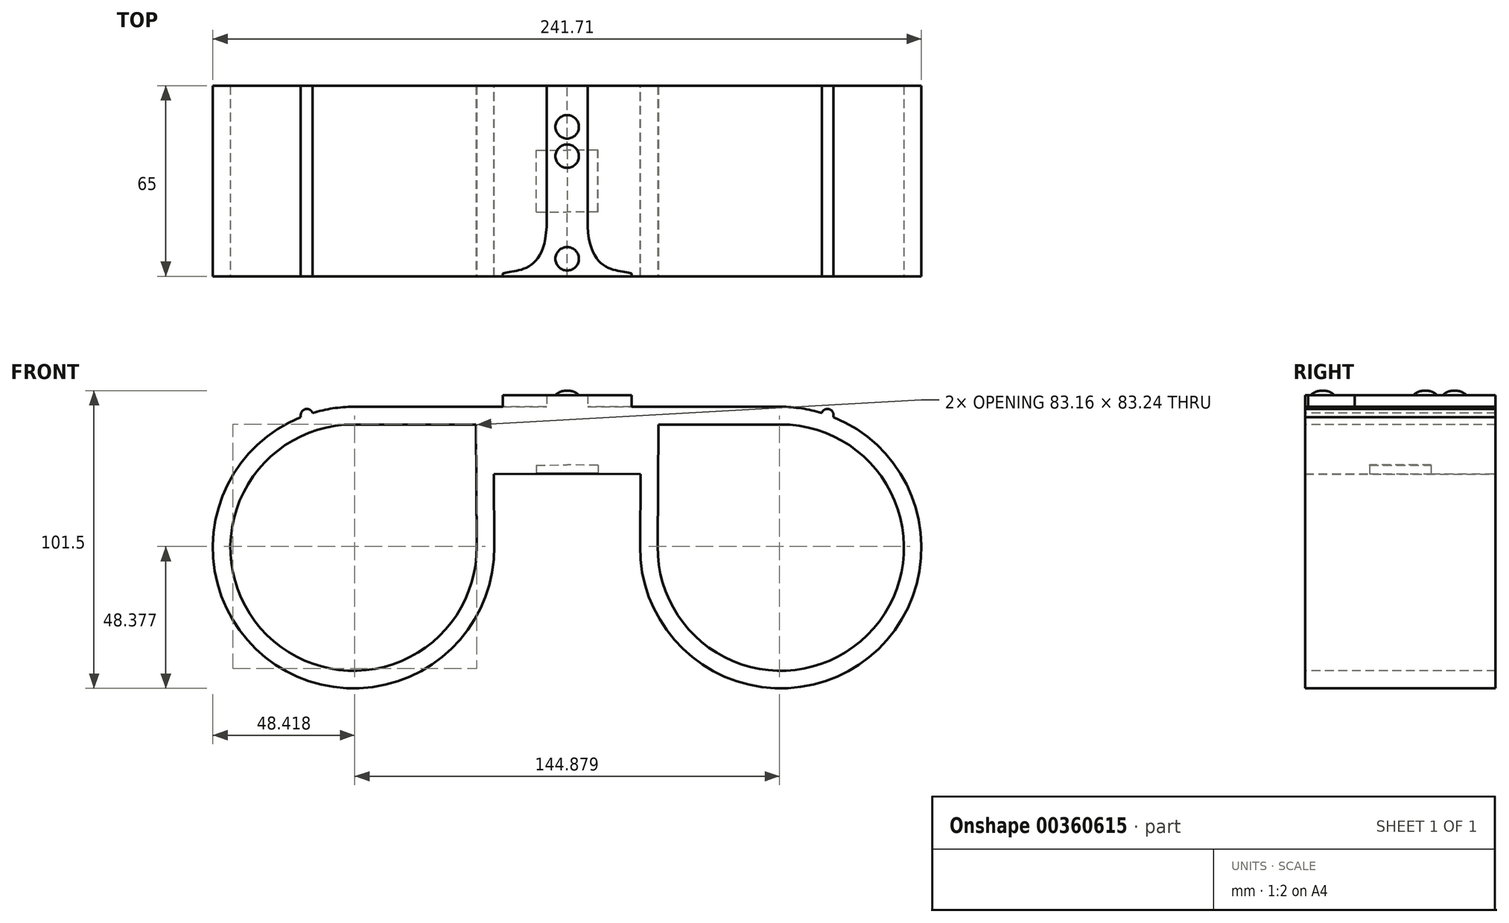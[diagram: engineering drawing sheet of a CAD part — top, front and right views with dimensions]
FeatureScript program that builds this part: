
annotation { "Feature Type Name" : "Feature", "Feature Type Description" : "" }
export const myFeature = defineFeature(function(context is Context, id is Id, definition is map)
    precondition{}
    {
        {
            var Q0;
            Q0=qCreatedBy(makeId("Front.planeOp"),FACE);
            var sketch = newSketch(context, id + "F0", { "sketchPlane" : qUnion([Q0])});
            skLineSegment(sketch, "E0", {"start": v(42.77, 0.25) * mm, "end": v(42.77, 23.06) * mm});
            skLineSegment(sketch, "E1", {"start": v(42.77, 23.06) * mm, "end": v(-30.09, 23.06) * mm});
            skLineSegment(sketch, "E2", {"start": v(-30.09, 23.06) * mm, "end": v(-30.09, -24.94) * mm});
            skLineSegment(sketch, "E3", {"start": v(0, 0) * mm, "end": v(17.77, 0.1) * mm});
            skCircle(sketch, "E4", {"center": v(-30.09, -24.94) * mm, "radius": 48 * mm});
            skLineSegment(sketch, "E5", {"start": v(17.91, -24.83) * mm, "end": v(17.77, 0.12) * mm});
            skPoint(sketch, "E5.endSnap0", {"position": v(21.38, 0.12) * mm});
            skLineSegment(sketch, "E6", {"start": v(17.77, 0.1) * mm, "end": v(42.77, 0.25) * mm});
            skSolve(sketch);
        }
        {
            var Q0;
            Q0 = qSketchRegion(id + "F0", true);
            extrude(context, id + "F1", {"entities" : qUnion([Q0]), "depth" : 65 * mm});
        }
        {
            var Q0;
            Q0=makeQuery(id+"F1.opExtrude","CAP_FACE",FACE,{"disambiguationData":[OSD([sQuery(id+"F0.wireOp",EDGE,"E0"),sQuery(id+"F0.wireOp",EDGE,"E1"),sQuery(id+"F0.wireOp",EDGE,"E4"),sQuery(id+"F0.wireOp",EDGE,"E5"),sQuery(id+"F0.wireOp",EDGE,"E6")])],"isStart":false});
            var sketch = newSketch(context, id + "F2", { "sketchPlane" : qUnion([Q0])});
            skCircle(sketch, "E7", {"center": v(-30.09, -24.94) * mm, "radius": 48 * mm});
            skPoint(sketch, "E7.first.point", {"position": v(-58.46, 13.77) * mm});
            skPoint(sketch, "E7.second.point", {"position": v(2.11, -60.54) * mm});
            skPoint(sketch, "E7.third.point", {"position": v(-63.88, -59.04) * mm});
            skLineSegment(sketch, "E8", {"start": v(-30.09, -24.94) * mm, "end": v(-30.09, 32.11) * mm, "construction": true});
            skLineSegment(sketch, "E9", {"start": v(-30.09, -24.94) * mm, "end": v(-44.09, -24.94) * mm});
            skLineSegment(sketch, "E10", {"start": v(-44.09, -24.94) * mm, "end": v(-44.09, 50.31) * mm});
            skLineSegment(sketch, "E11", {"start": v(-44.09, -24.94) * mm, "end": v(-48.09, -24.94) * mm});
            skLineSegment(sketch, "E12", {"start": v(-48.09, -24.94) * mm, "end": v(-48.09, 37.37) * mm});
            skCircle(sketch, "E13", {"center": v(-30.09, -24.94) * mm, "radius": 50 * mm});
            skSolve(sketch);
        }
        {
            var Q0;
            {var subQ0=sQuery(id+"F2.wireOp",EDGE,"E10");var subQ1=sQuery(id+"F2.wireOp",EDGE,"E7");var subQ2=makeQuery(id+"F2.imprint","INTERSECT",VERTEX,{"derivedFrom":[subQ1,subQ0]});Q0=makeQuery(id+"F2.imprint","IMPRINT",FACE,{"disambiguationData":[TD([[makeQuery(id+"F2.imprint","IMPRINT",EDGE,{"disambiguationData":[TD([[subQ2,-1.0]])],"derivedFrom":subQ1}),-1.0]])]});}
            extrude(context, id + "F3", {"entities" : qUnion([Q0]), "operationType" : NewBodyOperationType.ADD, "oppositeDirection" : true, "depth" : 65 * mm});
        }
        {
            var Q0;
            Q0=makeQuery(id+"F3.opExtrude","SWEPT_EDGE",EDGE,{"disambiguationData":[OSD([sQuery(id+"F2.wireOp",EDGE,"E10"),sQuery(id+"F2.wireOp",EDGE,"E13")])]});
            var Q1;
            Q1=makeQuery(id+"F3.opExtrude","SWEPT_EDGE",EDGE,{"disambiguationData":[OSD([sQuery(id+"F2.wireOp",EDGE,"E12"),sQuery(id+"F2.wireOp",EDGE,"E13")])]});
            fillet(context, id + "F4", {"entities" : qUnion([Q0, Q1]), "radius" : 2 * mm, "tangentPropagation" : true, "allowEdgeOverflow" : false});
        }
        {
            var Q0;
            Q0=makeQuery(id+"F1.opExtrude","SWEPT_FACE",FACE,{"disambiguationData":[OSD([sQuery(id+"F0.wireOp",EDGE,"E6")])]});
            var sketch = newSketch(context, id + "F5", { "sketchPlane" : qUnion([Q0])});
            skLineSegment(sketch, "E14.bottom", {"start": v(32.27, 43) * mm, "end": v(53.27, 43) * mm});
            skLineSegment(sketch, "E14.top", {"start": v(32.27, 22) * mm, "end": v(53.27, 22) * mm});
            skLineSegment(sketch, "E14.left", {"start": v(32.27, 43) * mm, "end": v(32.27, 22) * mm});
            skLineSegment(sketch, "E14.right", {"start": v(53.27, 43) * mm, "end": v(53.27, 22) * mm});
            skPoint(sketch, "E14.middle", {"position": v(42.77, 32.5) * mm});
            skSolve(sketch);
        }
        {
            var Q0;
            Q0 = qSketchRegion(id + "F5", true);
            extrude(context, id + "F6", {"entities" : qUnion([Q0]), "operationType" : NewBodyOperationType.REMOVE, "oppositeDirection" : true, "depth" : 3 * mm});
        }
        {
            var Q0;
            {var subQ0=sQuery(id+"F2.wireOp",EDGE,"E13");var subQ1=sQuery(id+"F2.wireOp",EDGE,"E12");var subQ2=sQuery(id+"F2.wireOp",EDGE,"E10");var subQ3=sQuery(id+"F2.wireOp",EDGE,"E7");Q0=makeQuery(id+"FzD17S7ChQ9cvDI_1.26.F3.boolean.opBoolean","MERGE",FACE,{"derivedFrom":[makeQuery(id+"FzD17S7ChQ9cvDI_1.25.F3.boolean.opBoolean","MERGE",FACE,{"derivedFrom":[makeQuery(id+"FzD17S7ChQ9cvDI_1.24.F3.boolean.opBoolean","MERGE",FACE,{"derivedFrom":[makeQuery(id+"FzD17S7ChQ9cvDI_1.23.F3.boolean.opBoolean","MERGE",FACE,{"derivedFrom":[makeQuery(id+"FzD17S7ChQ9cvDI_1.22.F3.boolean.opBoolean","MERGE",FACE,{"derivedFrom":[makeQuery(id+"FzD17S7ChQ9cvDI_1.21.F3.boolean.opBoolean","MERGE",FACE,{"derivedFrom":[makeQuery(id+"FzD17S7ChQ9cvDI_1.20.F3.boolean.opBoolean","MERGE",FACE,{"derivedFrom":[makeQuery(id+"FzD17S7ChQ9cvDI_1.19.F3.boolean.opBoolean","MERGE",FACE,{"derivedFrom":[makeQuery(id+"FzD17S7ChQ9cvDI_1.18.F3.boolean.opBoolean","MERGE",FACE,{"derivedFrom":[makeQuery(id+"FzD17S7ChQ9cvDI_1.17.F3.boolean.opBoolean","MERGE",FACE,{"derivedFrom":[makeQuery(id+"FzD17S7ChQ9cvDI_1.16.F3.boolean.opBoolean","MERGE",FACE,{"derivedFrom":[makeQuery(id+"FzD17S7ChQ9cvDI_1.15.F3.boolean.opBoolean","MERGE",FACE,{"derivedFrom":[makeQuery(id+"FzD17S7ChQ9cvDI_1.14.F3.boolean.opBoolean","MERGE",FACE,{"derivedFrom":[makeQuery(id+"FzD17S7ChQ9cvDI_1.13.F3.boolean.opBoolean","MERGE",FACE,{"derivedFrom":[makeQuery(id+"FzD17S7ChQ9cvDI_1.12.F3.boolean.opBoolean","MERGE",FACE,{"derivedFrom":[makeQuery(id+"FzD17S7ChQ9cvDI_1.11.F3.boolean.opBoolean","MERGE",FACE,{"derivedFrom":[makeQuery(id+"FzD17S7ChQ9cvDI_1.10.F3.boolean.opBoolean","MERGE",FACE,{"derivedFrom":[makeQuery(id+"FzD17S7ChQ9cvDI_1.9.F3.boolean.opBoolean","MERGE",FACE,{"derivedFrom":[makeQuery(id+"FzD17S7ChQ9cvDI_1.8.F3.boolean.opBoolean","MERGE",FACE,{"derivedFrom":[makeQuery(id+"FzD17S7ChQ9cvDI_1.7.F3.boolean.opBoolean","MERGE",FACE,{"derivedFrom":[makeQuery(id+"FzD17S7ChQ9cvDI_1.6.F3.boolean.opBoolean","MERGE",FACE,{"derivedFrom":[makeQuery(id+"FzD17S7ChQ9cvDI_1.5.F3.boolean.opBoolean","MERGE",FACE,{"derivedFrom":[makeQuery(id+"FzD17S7ChQ9cvDI_1.4.F3.boolean.opBoolean","MERGE",FACE,{"derivedFrom":[makeQuery(id+"FzD17S7ChQ9cvDI_1.3.F3.boolean.opBoolean","MERGE",FACE,{"derivedFrom":[makeQuery(id+"FzD17S7ChQ9cvDI_1.2.F3.boolean.opBoolean","MERGE",FACE,{"derivedFrom":[makeQuery(id+"FzD17S7ChQ9cvDI_1.1.F3.boolean.opBoolean","MERGE",FACE,{"derivedFrom":[makeQuery(id+"F3.boolean.opBoolean","MERGE",FACE,{"derivedFrom":[makeQuery(id+"F1.opExtrude","CAP_FACE",FACE,{"disambiguationData":[OSD([sQuery(id+"F0.wireOp",EDGE,"E0"),sQuery(id+"F0.wireOp",EDGE,"E1"),sQuery(id+"F0.wireOp",EDGE,"E4"),sQuery(id+"F0.wireOp",EDGE,"E5"),sQuery(id+"F0.wireOp",EDGE,"E6")])],"isStart":false}),makeQuery(id+"F3.opExtrude","CAP_FACE",FACE,{"disambiguationData":[OSD([subQ3,subQ2,subQ1,subQ0])],"isStart":true})]}),makeQuery(id+"FzD17S7ChQ9cvDI_1.1.F3.opExtrude","CAP_FACE",FACE,{"disambiguationData":[OSD([subQ3,subQ2,subQ1,subQ0])],"isStart":true})]}),makeQuery(id+"FzD17S7ChQ9cvDI_1.2.F3.opExtrude","CAP_FACE",FACE,{"disambiguationData":[OSD([subQ3,subQ2,subQ1,subQ0])],"isStart":true})]}),makeQuery(id+"FzD17S7ChQ9cvDI_1.3.F3.opExtrude","CAP_FACE",FACE,{"disambiguationData":[OSD([subQ3,subQ2,subQ1,subQ0])],"isStart":true})]}),makeQuery(id+"FzD17S7ChQ9cvDI_1.4.F3.opExtrude","CAP_FACE",FACE,{"disambiguationData":[OSD([subQ3,subQ2,subQ1,subQ0])],"isStart":true})]}),makeQuery(id+"FzD17S7ChQ9cvDI_1.5.F3.opExtrude","CAP_FACE",FACE,{"disambiguationData":[OSD([subQ3,subQ2,subQ1,subQ0])],"isStart":true})]}),makeQuery(id+"FzD17S7ChQ9cvDI_1.6.F3.opExtrude","CAP_FACE",FACE,{"disambiguationData":[OSD([subQ3,subQ2,subQ1,subQ0])],"isStart":true})]}),makeQuery(id+"FzD17S7ChQ9cvDI_1.7.F3.opExtrude","CAP_FACE",FACE,{"disambiguationData":[OSD([subQ3,subQ2,subQ1,subQ0])],"isStart":true})]}),makeQuery(id+"FzD17S7ChQ9cvDI_1.8.F3.opExtrude","CAP_FACE",FACE,{"disambiguationData":[OSD([subQ3,subQ2,subQ1,subQ0])],"isStart":true})]}),makeQuery(id+"FzD17S7ChQ9cvDI_1.9.F3.opExtrude","CAP_FACE",FACE,{"disambiguationData":[OSD([subQ3,subQ2,subQ1,subQ0])],"isStart":true})]}),makeQuery(id+"FzD17S7ChQ9cvDI_1.10.F3.opExtrude","CAP_FACE",FACE,{"disambiguationData":[OSD([subQ3,subQ2,subQ1,subQ0])],"isStart":true})]}),makeQuery(id+"FzD17S7ChQ9cvDI_1.11.F3.opExtrude","CAP_FACE",FACE,{"disambiguationData":[OSD([subQ3,subQ2,subQ1,subQ0])],"isStart":true})]}),makeQuery(id+"FzD17S7ChQ9cvDI_1.12.F3.opExtrude","CAP_FACE",FACE,{"disambiguationData":[OSD([subQ3,subQ2,subQ1,subQ0])],"isStart":true})]}),makeQuery(id+"FzD17S7ChQ9cvDI_1.13.F3.opExtrude","CAP_FACE",FACE,{"disambiguationData":[OSD([subQ3,subQ2,subQ1,subQ0])],"isStart":true})]}),makeQuery(id+"FzD17S7ChQ9cvDI_1.14.F3.opExtrude","CAP_FACE",FACE,{"disambiguationData":[OSD([subQ3,subQ2,subQ1,subQ0])],"isStart":true})]}),makeQuery(id+"FzD17S7ChQ9cvDI_1.15.F3.opExtrude","CAP_FACE",FACE,{"disambiguationData":[OSD([subQ3,subQ2,subQ1,subQ0])],"isStart":true})]}),makeQuery(id+"FzD17S7ChQ9cvDI_1.16.F3.opExtrude","CAP_FACE",FACE,{"disambiguationData":[OSD([subQ3,subQ2,subQ1,subQ0])],"isStart":true})]}),makeQuery(id+"FzD17S7ChQ9cvDI_1.17.F3.opExtrude","CAP_FACE",FACE,{"disambiguationData":[OSD([subQ3,subQ2,subQ1,subQ0])],"isStart":true})]}),makeQuery(id+"FzD17S7ChQ9cvDI_1.18.F3.opExtrude","CAP_FACE",FACE,{"disambiguationData":[OSD([subQ3,subQ2,subQ1,subQ0])],"isStart":true})]}),makeQuery(id+"FzD17S7ChQ9cvDI_1.19.F3.opExtrude","CAP_FACE",FACE,{"disambiguationData":[OSD([subQ3,subQ2,subQ1,subQ0])],"isStart":true})]}),makeQuery(id+"FzD17S7ChQ9cvDI_1.20.F3.opExtrude","CAP_FACE",FACE,{"disambiguationData":[OSD([subQ3,subQ2,subQ1,subQ0])],"isStart":true})]}),makeQuery(id+"FzD17S7ChQ9cvDI_1.21.F3.opExtrude","CAP_FACE",FACE,{"disambiguationData":[OSD([subQ3,subQ2,subQ1,subQ0])],"isStart":true})]}),makeQuery(id+"FzD17S7ChQ9cvDI_1.22.F3.opExtrude","CAP_FACE",FACE,{"disambiguationData":[OSD([subQ3,subQ2,subQ1,subQ0])],"isStart":true})]}),makeQuery(id+"FzD17S7ChQ9cvDI_1.23.F3.opExtrude","CAP_FACE",FACE,{"disambiguationData":[OSD([subQ3,subQ2,subQ1,subQ0])],"isStart":true})]}),makeQuery(id+"FzD17S7ChQ9cvDI_1.24.F3.opExtrude","CAP_FACE",FACE,{"disambiguationData":[OSD([subQ3,subQ2,subQ1,subQ0])],"isStart":true})]}),makeQuery(id+"FzD17S7ChQ9cvDI_1.25.F3.opExtrude","CAP_FACE",FACE,{"disambiguationData":[OSD([subQ3,subQ2,subQ1,subQ0])],"isStart":true})]}),makeQuery(id+"FzD17S7ChQ9cvDI_1.26.F3.opExtrude","CAP_FACE",FACE,{"disambiguationData":[OSD([subQ3,subQ2,subQ1,subQ0])],"isStart":true})]});}
            var sketch = newSketch(context, id + "F7", { "sketchPlane" : qUnion([Q0])});
            skCircle(sketch, "E15", {"center": v(-30.09, -24.94) * mm, "radius": 48 * mm});
            skPoint(sketch, "E15.first.point", {"position": v(-61.66, 11.21) * mm});
            skPoint(sketch, "E15.second.point", {"position": v(2.56, -60.13) * mm});
            skPoint(sketch, "E15.third.point", {"position": v(-63.24, -59.66) * mm});
            skArc(sketch, "E16.0", {"start": v(-5.97, -59.33) * mm, "mid": v(-3.45, -57.41) * mm, "end": v(-1.07, -55.3) * mm});
            skArc(sketch, "E16.1", {"start": v(-11.42, -62.57) * mm, "mid": v(-8.64, -61.05) * mm, "end": v(-5.97, -59.33) * mm});
            skArc(sketch, "E16.2", {"start": v(-17.3, -64.95) * mm, "mid": v(-14.31, -63.87) * mm, "end": v(-11.42, -62.57) * mm});
            skArc(sketch, "E16.3", {"start": v(-23.46, -66.42) * mm, "mid": v(-20.35, -65.8) * mm, "end": v(-17.3, -64.95) * mm});
            skArc(sketch, "E16.4", {"start": v(-29.78, -66.94) * mm, "mid": v(-26.6, -66.8) * mm, "end": v(-23.46, -66.42) * mm});
            skArc(sketch, "E16.5", {"start": v(-36.1, -66.51) * mm, "mid": v(-32.95, -66.85) * mm, "end": v(-29.78, -66.94) * mm});
            skArc(sketch, "E16.6", {"start": v(-42.29, -65.13) * mm, "mid": v(-39.22, -65.94) * mm, "end": v(-36.1, -66.51) * mm});
            skArc(sketch, "E16.7", {"start": v(-62.55, 1.7) * mm, "mid": v(-64.47, -0.82) * mm, "end": v(-66.2, -3.48) * mm});
            skArc(sketch, "E16.8", {"start": v(-58.17, 6.29) * mm, "mid": v(-60.45, 4.08) * mm, "end": v(-62.55, 1.7) * mm});
            skArc(sketch, "E16.9", {"start": v(-53.15, 10.16) * mm, "mid": v(-55.74, 8.32) * mm, "end": v(-58.17, 6.29) * mm});
            skArc(sketch, "E16.10", {"start": v(-47.61, 13.23) * mm, "mid": v(-50.44, 11.8) * mm, "end": v(-53.15, 10.16) * mm});
            skArc(sketch, "E16.11", {"start": v(-41.67, 15.43) * mm, "mid": v(-44.68, 14.44) * mm, "end": v(-47.61, 13.23) * mm});
            skArc(sketch, "E16.12", {"start": v(-35.46, 16.71) * mm, "mid": v(-38.59, 16.19) * mm, "end": v(-41.67, 15.43) * mm});
            skArc(sketch, "E16.13", {"start": v(3.16, -50.6) * mm, "mid": v(9.73, -38.31) * mm, "end": v(11.9, -24.55) * mm});
            skLineSegment(sketch, "E16.14", {"start": v(11.9, -24.55) * mm, "end": v(11.67, 17.06) * mm});
            skLineSegment(sketch, "E16.15", {"start": v(11.67, 17.06) * mm, "end": v(-30.09, 17.06) * mm});
            skArc(sketch, "E16.16", {"start": v(-30.09, 17.06) * mm, "mid": v(-32.78, 16.97) * mm, "end": v(-35.46, 16.71) * mm});
            skArc(sketch, "E16.17", {"start": v(-66.2, -3.48) * mm, "mid": v(-67.7, -6.27) * mm, "end": v(-69, -9.16) * mm});
            skArc(sketch, "E16.18", {"start": v(-69, -9.16) * mm, "mid": v(-70.09, -12.14) * mm, "end": v(-70.94, -15.2) * mm});
            skArc(sketch, "E16.19", {"start": v(-70.94, -15.2) * mm, "mid": v(-71.56, -18.3) * mm, "end": v(-71.94, -21.45) * mm});
            skArc(sketch, "E16.20", {"start": v(-71.94, -21.45) * mm, "mid": v(-72.09, -24.62) * mm, "end": v(-72, -27.79) * mm});
            skArc(sketch, "E16.21", {"start": v(-72, -27.79) * mm, "mid": v(-71.66, -30.94) * mm, "end": v(-71.09, -34.06) * mm});
            skArc(sketch, "E16.22", {"start": v(-71.09, -34.06) * mm, "mid": v(-70.28, -37.13) * mm, "end": v(-69.25, -40.13) * mm});
            skArc(sketch, "E16.23", {"start": v(-69.25, -40.13) * mm, "mid": v(-68, -43.04) * mm, "end": v(-66.52, -45.85) * mm});
            skArc(sketch, "E16.24", {"start": v(-1.07, -55.3) * mm, "mid": v(1.13, -53.03) * mm, "end": v(3.16, -50.6) * mm});
            skArc(sketch, "E16.25", {"start": v(-66.52, -45.85) * mm, "mid": v(-64.84, -48.54) * mm, "end": v(-62.96, -51.09) * mm});
            skArc(sketch, "E16.26", {"start": v(-62.96, -51.09) * mm, "mid": v(-60.9, -53.5) * mm, "end": v(-58.65, -55.74) * mm});
            skArc(sketch, "E16.27", {"start": v(-58.65, -55.74) * mm, "mid": v(-56.24, -57.8) * mm, "end": v(-53.7, -59.68) * mm});
            skArc(sketch, "E16.28", {"start": v(-53.7, -59.68) * mm, "mid": v(-51, -61.37) * mm, "end": v(-48.2, -62.84) * mm});
            skArc(sketch, "E16.29", {"start": v(-48.2, -62.84) * mm, "mid": v(-45.28, -64.1) * mm, "end": v(-42.29, -65.13) * mm});
            skSolve(sketch);
        }
        {
            var Q0;
            Q0=makeQuery(id+"F7.imprint","IMPRINT",FACE,{"disambiguationData":[TD([[makeQuery(id+"F7.imprint","IMPRINT",EDGE,{"derivedFrom":sQuery(id+"F7.wireOp",EDGE,"E16.0")}),1.0]])]});
            var Q1;
            {var subQ0=sQuery(id+"F7.wireOp",EDGE,"E16.14");var subQ1=sQuery(id+"F7.wireOp",EDGE,"E15");var subQ2=makeQuery(id+"F7.imprint","INTERSECT",VERTEX,{"derivedFrom":[subQ1,subQ0]});Q1=makeQuery(id+"F7.imprint","IMPRINT",FACE,{"disambiguationData":[TD([[makeQuery(id+"F7.imprint","IMPRINT",EDGE,{"disambiguationData":[TD([[subQ2,-1.0]])],"derivedFrom":subQ1}),-1.0]])]});}
            extrude(context, id + "F8", {"entities" : qUnion([Q0, Q1]), "operationType" : NewBodyOperationType.REMOVE, "oppositeDirection" : true, "depth" : 75 * mm});
        }
        {
            var Q0;
            Q0=makeQuery(id+"F1.opExtrude","SWEPT_FACE",FACE,{"disambiguationData":[OSD([sQuery(id+"F0.wireOp",EDGE,"E1")])]});
            var sketch = newSketch(context, id + "F9", { "sketchPlane" : qUnion([Q0])});
            skLineSegment(sketch, "E17.bottom", {"start": v(42.77, -65) * mm, "end": v(20.77, -65) * mm});
            skLineSegment(sketch, "E17.top", {"start": v(42.77, -64) * mm, "end": v(20.77, -64) * mm});
            skLineSegment(sketch, "E17.left", {"start": v(42.77, -65) * mm, "end": v(42.77, -64) * mm});
            skLineSegment(sketch, "E17.right", {"start": v(20.77, -65) * mm, "end": v(20.77, -64) * mm});
            skLineSegment(sketch, "E18.bottom", {"start": v(42.77, 0) * mm, "end": v(35.77, 0) * mm});
            skLineSegment(sketch, "E18.top", {"start": v(42.77, -64) * mm, "end": v(35.77, -64) * mm});
            skLineSegment(sketch, "E18.left", {"start": v(42.77, 0) * mm, "end": v(42.77, -64) * mm});
            skLineSegment(sketch, "E18.right", {"start": v(35.77, 0) * mm, "end": v(35.77, -64) * mm});
            skFitSpline(sketch, "E19", {"points": [v(20.77, -64) * mm, v(35.77, -48.01) * mm], "startDerivative": vector(10.39, 4.39) * mm, "endDerivative": vector(2.48, 50.96) * mm});
            skSolve(sketch);
        }
        {
            var Q0;
            {var subQ1=sQuery(id+"F9.wireOp",EDGE,"E18.bottom");Q0=makeQuery(id+"F9.imprint","IMPRINT",FACE,{"disambiguationData":[TD([[makeQuery(id+"F9.imprint","IMPRINT",EDGE,{"derivedFrom":subQ1}),1.0]])]});}
            var Q1;
            {var subQ0=sQuery(id+"F9.wireOp",EDGE,"E17.top");Q1=makeQuery(id+"F9.imprint","IMPRINT",FACE,{"disambiguationData":[TD([[makeQuery(id+"F9.imprint","IMPRINT",EDGE,{"derivedFrom":subQ0}),-1.0]])]});}
            var Q2;
            Q2=makeQuery(id+"F9.imprint","IMPRINT",FACE,{"disambiguationData":[TD([[makeQuery(id+"F9.imprint","IMPRINT",EDGE,{"derivedFrom":sQuery(id+"F9.wireOp",EDGE,"E17.bottom")}),-1.0]])]});
            extrude(context, id + "F10", {"entities" : qUnion([Q0, Q1, Q2]), "operationType" : NewBodyOperationType.ADD, "depth" : 4 * mm});
        }
        {
            var Q0;
            Q0=makeQuery(id+"F1.opExtrude","SWEPT_BODY",BODY,{"disambiguationData":[OSD([sQuery(id+"F0.wireOp",EDGE,"E0"),sQuery(id+"F0.wireOp",EDGE,"E1"),sQuery(id+"F0.wireOp",EDGE,"E3"),sQuery(id+"F0.wireOp",EDGE,"E4")])]});
            var Q1;
            Q1=makeQuery(id+"F1.opExtrude","SWEPT_FACE",FACE,{"disambiguationData":[OSD([sQuery(id+"F0.wireOp",EDGE,"E0")])]});
            mirror(context, id + "F11", {"operationType" : NewBodyOperationType.ADD, "entities" : qUnion([Q0]), "mirrorPlane" : qUnion([Q1])});
        }
        {
            var Q0;
            {var subQ0=makeQuery(id+"F10.opExtrude","CAP_FACE",FACE,{"disambiguationData":[OSD([sQuery(id+"F9.wireOp",EDGE,"E17.bottom"),sQuery(id+"F9.wireOp",EDGE,"E17.left"),sQuery(id+"F9.wireOp",EDGE,"E17.right"),sQuery(id+"F9.wireOp",EDGE,"E18.bottom"),sQuery(id+"F9.wireOp",EDGE,"E18.left"),sQuery(id+"F9.wireOp",EDGE,"E18.right"),sQuery(id+"F9.wireOp",EDGE,"E19")])],"isStart":false});Q0=makeQuery(id+"F11.boolean.opBoolean","MERGE",FACE,{"derivedFrom":[subQ0,makeQuery(id+"F11.opPattern","COPY",FACE,{"derivedFrom":subQ0,"instanceName":"1"})]});}
            var sketch = newSketch(context, id + "F12", { "sketchPlane" : qUnion([Q0])});
            skLineSegment(sketch, "E20", {"start": v(42.77, -65) * mm, "end": v(42.77, -59) * mm});
            skCircle(sketch, "E21", {"center": v(42.77, -59) * mm, "radius": 4 * mm});
            skLineSegment(sketch, "E22", {"start": v(42.77, -59) * mm, "end": v(42.77, -24) * mm});
            skPoint(sketch, "E22.endSnap0", {"position": v(49.77, -24) * mm});
            skCircle(sketch, "E23", {"center": v(42.77, -24) * mm, "radius": 4 * mm});
            skLineSegment(sketch, "E24", {"start": v(42.77, -24) * mm, "end": v(42.77, -14) * mm});
            skCircle(sketch, "E25", {"center": v(42.77, -14) * mm, "radius": 4 * mm});
            skSolve(sketch);
        }
        {
            var Q0;
            Q0 = qSketchRegion(id + "F12", true);
            extrude(context, id + "F13", {"entities" : qUnion([Q0]), "operationType" : NewBodyOperationType.ADD, "depth" : 1.5 * mm});
        }
        {
            var Q0;
            Q0=makeQuery(id+"F13.opExtrude","CAP_EDGE",EDGE,{"disambiguationData":[OSD([sQuery(id+"F12.wireOp",EDGE,"E21")])],"isStart":false});
            var Q1;
            Q1=makeQuery(id+"F13.opExtrude","CAP_EDGE",EDGE,{"disambiguationData":[OSD([sQuery(id+"F12.wireOp",EDGE,"E23")])],"isStart":false});
            var Q2;
            Q2=makeQuery(id+"F13.opExtrude","CAP_EDGE",EDGE,{"disambiguationData":[OSD([sQuery(id+"F12.wireOp",EDGE,"E25")])],"isStart":false});
            fillet(context, id + "F14", {"entities" : qUnion([Q0, Q1, Q2]), "radius" : 5 * mm, "tangentPropagation" : true, "allowEdgeOverflow" : false});
        }
    });
